# Revit family: QF_GIORIK_SEMG101W_SEPG101W_SETG101W_SEHG101W
name_source: partatom
category: Specialty Equipment
revit_build: Autodesk Revit 2014 (Build: 20140709_2115(x64)
units: mm (PartAtom-declared; Revit-internal decimal feet)

## types (4) — shared parameters
Assembly Code = E1090320
Cold Water Connection Height = 115 mm  [stored 0.377297 ft]
Cold Water Size = 1"
Cold Water Temperature Recommended = 0 °C
Cycle = 50 Hz
FL Amps = 0 A
Gas Connection Height = 115 mm  [stored 0.377297 ft]
Gas Input = 19000 W
Gas KW = 19
Gas Size = 1"
HP = 0
Indirect Waste Connection Height = 77 mm  [stored 0.252625 ft]
Indirect Waste Flow = 0.0 L/s
Indirect Waste Size = 2"
Manufacturer = GIORIK
Max Overcurrent Protection = 16 A
Min Ckt Ampacity = 0 A
Phase = 1
URL = www.giorik.com
Volts = 230 V
Waste Water Discharge Temperature = 0 °C
Weight in Pounds = 392.423

## per-type parameters (varying)
| type | Apparent Power | Description | Digital control | Touch screen control | Watts |
| SEMG101W | 1700 VA | GAS OVEN 10 GN 1/1 COMBINED CONVECTION/STEAM DIGITAL CONTROL BOARD - WITH HIGH EFFICIENCY BOILER | Yes | No | 1700 W |
| SEPG101W | 700 VA | GAS OVEN 10 GN 1/1 COMBINED CONVECTION/STEAM DIGITAL CONTROL | Yes | No | 700 W |
| SEHG101W | 1700 VA | GAS OVEN 10 GN 1/1 COMBINED CONVECTION/STEAM TOUCH SCREEN CONTROL - WITH HIGH EFFICIENCY BOILER | No | Yes | 1700 W |
| SETG101W | 700 VA | GAS OVEN 10 GN 1/1 COMBINED CONVECTION/STEAM TOUCH SCREEN CONTROL | No | Yes | 700 W |

note: column(s) folded — value = type name in every type: Model

note: [stored X ft] marks values corroborated as IEEE doubles in the binary element streams (Revit-internal decimal feet)

## geometry (parser evidence)
native form markers: Blend x8, Sweep x1
no freeform markers — native parametric forms only
